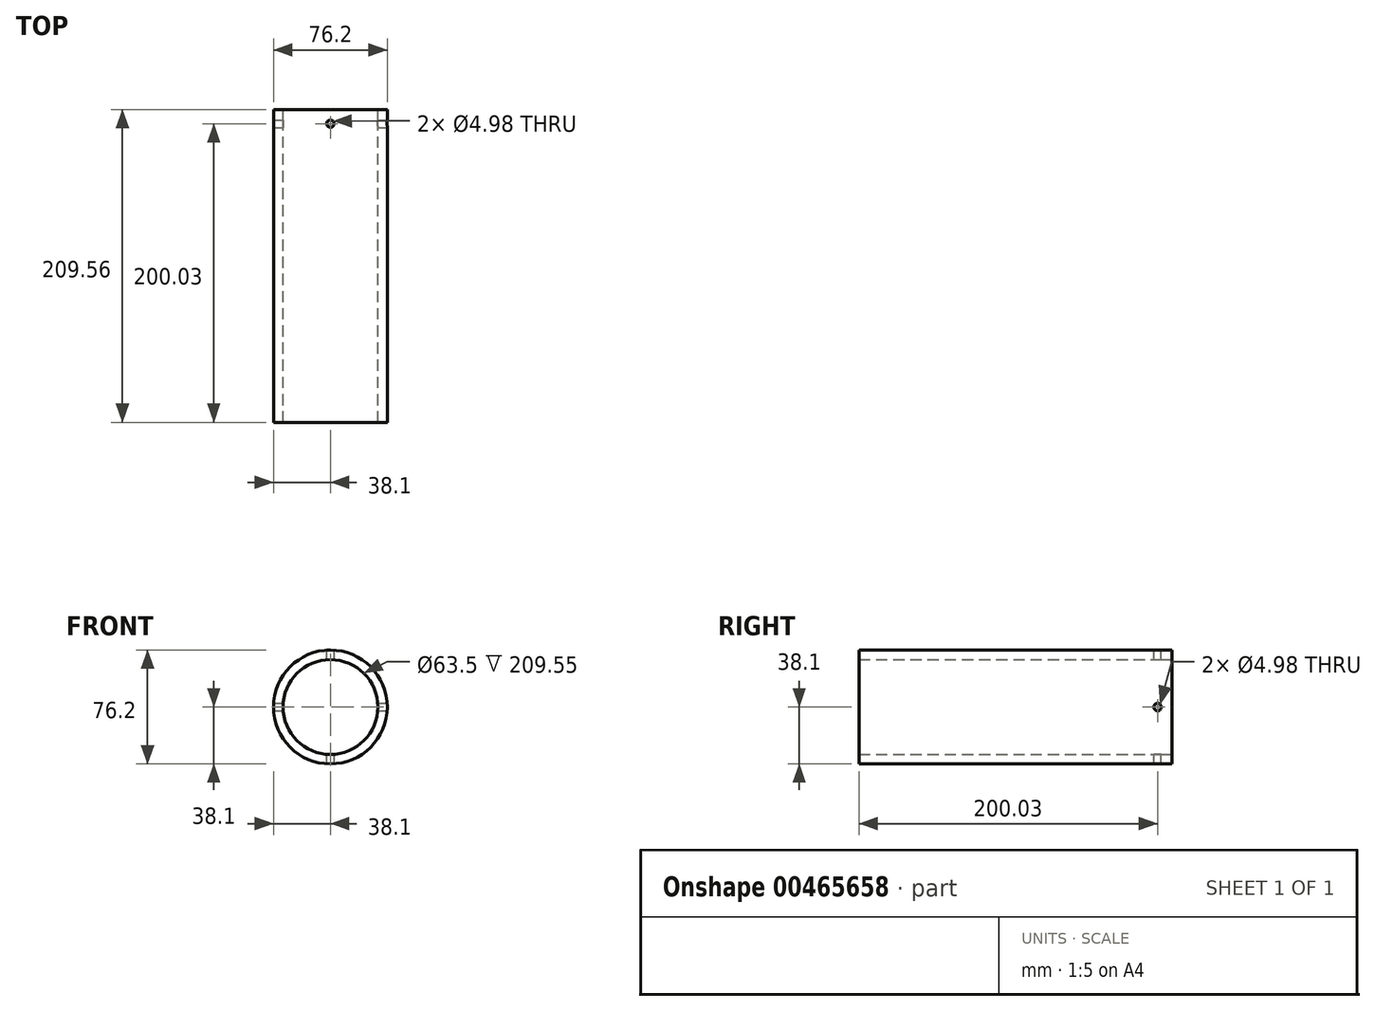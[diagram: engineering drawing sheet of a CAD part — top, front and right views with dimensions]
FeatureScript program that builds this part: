
annotation { "Feature Type Name" : "Feature", "Feature Type Description" : "" }
export const myFeature = defineFeature(function(context is Context, id is Id, definition is map)
    precondition{}
    {
        {
            var Q0;
            Q0=qCreatedBy(makeId("Front.planeOp"),FACE);
            var sketch = newSketch(context, id + "F0", { "sketchPlane" : qUnion([Q0])});
            skCircle(sketch, "E0", {"center": v(0, 0) * mm, "radius": 38.1 * mm});
            skCircle(sketch, "E1.0", {"center": v(0, 0) * mm, "radius": 31.75 * mm});
            skSolve(sketch);
        }
        {
            var Q0;
            Q0=makeQuery(id+"F0.imprint","IMPRINT",FACE,{"disambiguationData":[TD([[makeQuery(id+"F0.imprint","IMPRINT",EDGE,{"derivedFrom":sQuery(id+"F0.wireOp",EDGE,"E0")}),1.0]])]});
            extrude(context, id + "F1", {"entities" : qUnion([Q0]), "endBound" : BoundingType.SYMMETRIC, "depth" : 209.55 * mm});
        }
        {
            var Q0;
            Q0=qCreatedBy(makeId("Right.planeOp"),FACE);
            var sketch = newSketch(context, id + "F2", { "sketchPlane" : qUnion([Q0])});
            skLineSegment(sketch, "E2", {"start": v(95.25, 48.75) * mm, "end": v(95.25, -60.28) * mm, "construction": true});
            skLineSegment(sketch, "E3", {"start": v(122.14, 0) * mm, "end": v(-148.44, 0) * mm, "construction": true});
            skCircle(sketch, "E4", {"center": v(95.25, 0) * mm, "radius": 2.49 * mm});
            skLineSegment(sketch, "E5.MirrorCS", {"start": v(-95.25, 48.75) * mm, "end": v(-95.25, -60.28) * mm, "construction": true});
            skCircle(sketch, "E6.MirrorC", {"center": v(-95.25, 0) * mm, "radius": 2.49 * mm});
            skSolve(sketch);
        }
        {
            var Q0;
            Q0=makeQuery(id+"F2.imprint","IMPRINT",FACE,{"disambiguationData":[TD([[makeQuery(id+"F2.imprint","IMPRINT",EDGE,{"derivedFrom":sQuery(id+"F2.wireOp",EDGE,"E4")}),1.0]])]});
            var Q1;
            Q1=makeQuery(id+"F2.imprint","IMPRINT",FACE,{"disambiguationData":[TD([[makeQuery(id+"F2.imprint","IMPRINT",EDGE,{"derivedFrom":sQuery(id+"F2.wireOp",EDGE,"E6.MirrorC")}),-1.0]])]});
            extrude(context, id + "F3", {"entities" : qUnion([Q0, Q1]), "operationType" : NewBodyOperationType.REMOVE, "endBound" : BoundingType.SYMMETRIC, "oppositeDirection" : true, "depth" : 203.2 * mm});
        }
        {
            var Q0;
            Q0=qCreatedBy(makeId("Top.planeOp"),FACE);
            var sketch = newSketch(context, id + "F4", { "sketchPlane" : qUnion([Q0])});
            skLineSegment(sketch, "E7", {"start": v(-55.77, 95.25) * mm, "end": v(66.58, 95.25) * mm, "construction": true});
            skLineSegment(sketch, "E8", {"start": v(0, 124.66) * mm, "end": v(0, -132.95) * mm, "construction": true});
            skCircle(sketch, "E9", {"center": v(0, 95.25) * mm, "radius": 2.49 * mm});
            skCircle(sketch, "E10.MirrorC", {"center": v(0, -95.25) * mm, "radius": 2.49 * mm});
            skLineSegment(sketch, "E11.MirrorCS", {"start": v(-55.77, -95.25) * mm, "end": v(66.58, -95.25) * mm, "construction": true});
            skSolve(sketch);
        }
        {
            var Q0;
            Q0=makeQuery(id+"F4.imprint","IMPRINT",FACE,{"disambiguationData":[TD([[makeQuery(id+"F4.imprint","IMPRINT",EDGE,{"derivedFrom":sQuery(id+"F4.wireOp",EDGE,"E9")}),1.0]])]});
            var Q1;
            Q1=makeQuery(id+"F4.imprint","IMPRINT",FACE,{"disambiguationData":[TD([[makeQuery(id+"F4.imprint","IMPRINT",EDGE,{"derivedFrom":sQuery(id+"F4.wireOp",EDGE,"E10.MirrorC")}),-1.0]])]});
            extrude(context, id + "F5", {"entities" : qUnion([Q0, Q1]), "operationType" : NewBodyOperationType.REMOVE, "endBound" : BoundingType.SYMMETRIC, "oppositeDirection" : true, "depth" : 203.2 * mm});
        }
    });
